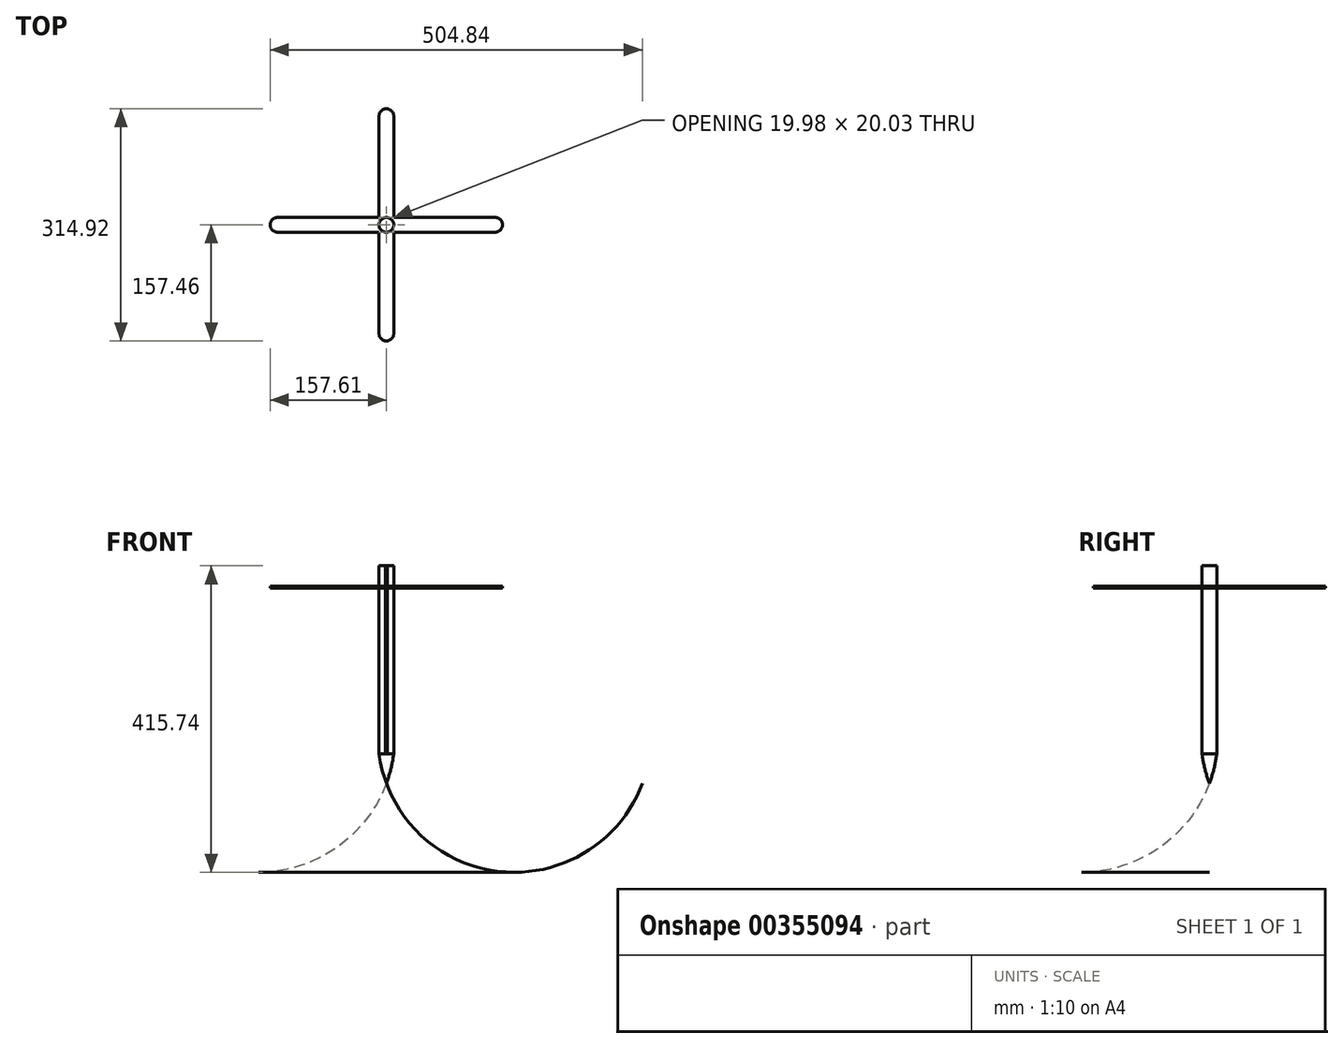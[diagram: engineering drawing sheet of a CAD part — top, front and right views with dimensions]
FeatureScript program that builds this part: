
annotation { "Feature Type Name" : "Feature", "Feature Type Description" : "" }
export const myFeature = defineFeature(function(context is Context, id is Id, definition is map)
    precondition{}
    {
        {
            var Q0;
            Q0=qCreatedBy(makeId("Top.planeOp"),FACE);
            var sketch = newSketch(context, id + "F0", { "sketchPlane" : qUnion([Q0])});
            skCircle(sketch, "E0", {"center": v(0, 0) * mm, "radius": 10.01 * mm});
            skLineSegment(sketch, "E1.bottom", {"start": v(0, 10.01) * mm, "end": v(147.64, 10.01) * mm});
            skLineSegment(sketch, "E1.top", {"start": v(0, -9.92) * mm, "end": v(147.64, -9.92) * mm});
            skLineSegment(sketch, "E1.left", {"start": v(0, 10.01) * mm, "end": v(0, -9.92) * mm});
            skLineSegment(sketch, "E1.right", {"start": v(147.64, 10.01) * mm, "end": v(147.64, -9.92) * mm});
            skLineSegment(sketch, "E2.MirrorCS", {"start": v(0, 10.01) * mm, "end": v(-147.64, 10.01) * mm});
            skLineSegment(sketch, "E3.MirrorCS", {"start": v(0, -9.92) * mm, "end": v(-147.64, -9.92) * mm});
            skLineSegment(sketch, "E4.MirrorCS", {"start": v(-147.64, 10.01) * mm, "end": v(-147.64, -9.92) * mm});
            skLineSegment(sketch, "E5", {"start": v(-10.01, 0) * mm, "end": v(-10.01, 147.44) * mm});
            skLineSegment(sketch, "E6", {"start": v(-10.01, 147.44) * mm, "end": v(10.01, 147.44) * mm});
            skLineSegment(sketch, "E7", {"start": v(10.01, 147.44) * mm, "end": v(10.01, 0) * mm});
            skLineSegment(sketch, "E8.MirrorCS", {"start": v(10.01, 147.44) * mm, "end": v(-10.01, 147.44) * mm});
            skLineSegment(sketch, "E9.MirrorCS", {"start": v(-10.01, -147.44) * mm, "end": v(10.01, -147.44) * mm});
            skLineSegment(sketch, "E10.MirrorCS", {"start": v(10.01, -147.44) * mm, "end": v(10.01, 0) * mm});
            skLineSegment(sketch, "E11.MirrorCS", {"start": v(-10.01, 0) * mm, "end": v(-10.01, -147.44) * mm});
            skArc(sketch, "E12", {"start": v(-147.64, 10.01) * mm, "mid": v(-157.61, 0.05) * mm, "end": v(-147.64, -9.92) * mm});
            skArc(sketch, "E13", {"start": v(-10.01, -147.44) * mm, "mid": v(0, -157.46) * mm, "end": v(10.01, -147.44) * mm});
            skArc(sketch, "E14.MirrorCS", {"start": v(147.64, 10.01) * mm, "mid": v(157.61, 0.05) * mm, "end": v(147.64, -9.92) * mm});
            skArc(sketch, "E15.MirrorCS", {"start": v(-10.01, 147.44) * mm, "mid": v(0, 157.46) * mm, "end": v(10.01, 147.44) * mm});
            skSolve(sketch);
        }
        {
            var Q0;
            {var subQ0=sQuery(id+"F0.wireOp",EDGE,"E1.left");Q0=makeQuery(id+"F0.imprint","IMPRINT",FACE,{"disambiguationData":[TD([[makeQuery(id+"F0.imprint","IMPRINT",EDGE,{"derivedFrom":subQ0}),-1.0]])]});}
            var Q1;
            {var subQ0=sQuery(id+"F0.wireOp",EDGE,"E1.left");Q1=makeQuery(id+"F0.imprint","IMPRINT",FACE,{"disambiguationData":[TD([[makeQuery(id+"F0.imprint","IMPRINT",EDGE,{"derivedFrom":subQ0}),1.0]])]});}
            extrude(context, id + "F1", {"entities" : qUnion([Q0, Q1]), "depth" : 30 * mm, "hasSecondDirection" : true, "secondDirectionOppositeDirection" : true, "secondDirectionDepth" : 225 * mm});
        }
        {
            var Q0;
            {var subQ5=sQuery(id+"F0.wireOp",EDGE,"E9.MirrorCS");Q0=makeQuery(id+"F0.imprint","IMPRINT",FACE,{"disambiguationData":[TD([[makeQuery(id+"F0.imprint","IMPRINT",EDGE,{"derivedFrom":subQ5}),1.0]])]});}
            var Q1;
            Q1=makeQuery(id+"F0.imprint","IMPRINT",FACE,{"disambiguationData":[TD([[makeQuery(id+"F0.imprint","IMPRINT",EDGE,{"derivedFrom":sQuery(id+"F0.wireOp",EDGE,"E9.MirrorCS")}),-1.0]])]});
            var Q2;
            Q2=makeQuery(id+"F0.imprint","IMPRINT",FACE,{"disambiguationData":[TD([[makeQuery(id+"F0.imprint","IMPRINT",EDGE,{"derivedFrom":sQuery(id+"F0.wireOp",EDGE,"E1.right")}),1.0]])]});
            var Q3;
            {var subQ1=sQuery(id+"F0.wireOp",EDGE,"E1.right");Q3=makeQuery(id+"F0.imprint","IMPRINT",FACE,{"disambiguationData":[TD([[makeQuery(id+"F0.imprint","IMPRINT",EDGE,{"derivedFrom":subQ1}),-1.0]])]});}
            var Q4;
            {var subQ0=sQuery(id+"F0.wireOp",EDGE,"E4.MirrorCS");Q4=makeQuery(id+"F0.imprint","IMPRINT",FACE,{"disambiguationData":[TD([[makeQuery(id+"F0.imprint","IMPRINT",EDGE,{"derivedFrom":subQ0}),1.0]])]});}
            var Q5;
            {var subQ1=sQuery(id+"F0.wireOp",EDGE,"E6");Q5=makeQuery(id+"F0.imprint","IMPRINT",FACE,{"disambiguationData":[TD([[makeQuery(id+"F0.imprint","IMPRINT",EDGE,{"derivedFrom":subQ1}),-1.0]])]});}
            var Q6;
            Q6=makeQuery(id+"F0.imprint","IMPRINT",FACE,{"disambiguationData":[TD([[makeQuery(id+"F0.imprint","IMPRINT",EDGE,{"derivedFrom":sQuery(id+"F0.wireOp",EDGE,"E6")}),1.0]])]});
            var Q7;
            Q7=makeQuery(id+"F0.imprint","IMPRINT",FACE,{"disambiguationData":[TD([[makeQuery(id+"F0.imprint","IMPRINT",EDGE,{"derivedFrom":sQuery(id+"F0.wireOp",EDGE,"E4.MirrorCS")}),-1.0]])]});
            var Q8;
            {var subQ0=sQuery(id+"F0.wireOp",EDGE,"E1.bottom");var subQ3=sQuery(id+"F0.wireOp",EDGE,"E7");var subQ5=makeQuery(id+"F0.imprint","INTERSECT",VERTEX,{"derivedFrom":[subQ0,subQ3]});Q8=makeQuery(id+"F0.imprint","IMPRINT",FACE,{"disambiguationData":[TD([[makeQuery(id+"F0.imprint","IMPRINT",EDGE,{"disambiguationData":[TD([[subQ5,-1.0]])],"derivedFrom":subQ3}),-1.0]])]});}
            var Q9;
            {var subQ0=sQuery(id+"F0.wireOp",EDGE,"E2.MirrorCS");var subQ3=sQuery(id+"F0.wireOp",EDGE,"E5");var subQ5=makeQuery(id+"F0.imprint","INTERSECT",VERTEX,{"derivedFrom":[subQ0,subQ3]});Q9=makeQuery(id+"F0.imprint","IMPRINT",FACE,{"disambiguationData":[TD([[makeQuery(id+"F0.imprint","IMPRINT",EDGE,{"disambiguationData":[TD([[subQ5,1.0]])],"derivedFrom":subQ3}),-1.0]])]});}
            var Q10;
            {var subQ0=sQuery(id+"F0.wireOp",EDGE,"E11.MirrorCS");var subQ3=sQuery(id+"F0.wireOp",EDGE,"E3.MirrorCS");var subQ5=makeQuery(id+"F0.imprint","INTERSECT",VERTEX,{"derivedFrom":[subQ3,subQ0]});Q10=makeQuery(id+"F0.imprint","IMPRINT",FACE,{"disambiguationData":[TD([[makeQuery(id+"F0.imprint","IMPRINT",EDGE,{"disambiguationData":[TD([[subQ5,1.0]])],"derivedFrom":subQ3}),-1.0]])]});}
            var Q11;
            {var subQ0=sQuery(id+"F0.wireOp",EDGE,"E10.MirrorCS");var subQ3=sQuery(id+"F0.wireOp",EDGE,"E1.top");var subQ5=makeQuery(id+"F0.imprint","INTERSECT",VERTEX,{"derivedFrom":[subQ3,subQ0]});Q11=makeQuery(id+"F0.imprint","IMPRINT",FACE,{"disambiguationData":[TD([[makeQuery(id+"F0.imprint","IMPRINT",EDGE,{"disambiguationData":[TD([[subQ5,1.0]])],"derivedFrom":subQ3}),1.0]])]});}
            extrude(context, id + "F2", {"entities" : qUnion([Q0, Q1, Q2, Q3, Q4, Q5, Q6, Q7, Q8, Q9, Q10, Q11]), "operationType" : NewBodyOperationType.ADD, "depth" : 2 * mm});
        }
        {
            var Q0;
            Q0=qCreatedBy(makeId("Front.planeOp"),FACE);
            var sketch = newSketch(context, id + "F3", { "sketchPlane" : qUnion([Q0])});
            skLineSegment(sketch, "E16", {"start": v(0, -224.96) * mm, "end": v(0, -265.1) * mm});
            skLineSegment(sketch, "E17", {"start": v(0, -265.1) * mm, "end": v(-10, -225) * mm});
            skLineSegment(sketch, "E18", {"start": v(-10, -225) * mm, "end": v(0, -224.96) * mm});
            skArc(sketch, "E19", {"start": v(-10, -225) * mm, "mid": v(-6.13, -245.33) * mm, "end": v(0, -265.1) * mm});
            skSolve(sketch);
        }
        {
            var Q0;
            Q0=makeQuery(id+"F3.imprint","IMPRINT",FACE,{"disambiguationData":[TD([[makeQuery(id+"F3.imprint","IMPRINT",EDGE,{"derivedFrom":sQuery(id+"F3.wireOp",EDGE,"E16")}),-1.0]])]});
            var Q1;
            Q1=makeQuery(id+"F3.imprint","IMPRINT",FACE,{"disambiguationData":[TD([[makeQuery(id+"F3.imprint","IMPRINT",EDGE,{"derivedFrom":sQuery(id+"F3.wireOp",EDGE,"E17")}),1.0]])]});
            var Q2;
            Q2=sQuery(id+"F3.wireOp",EDGE,"E16");
            revolve(context, id + "F4", {"operationType" : NewBodyOperationType.ADD, "entities" : qUnion([Q0, Q1]), "axis" : qUnion([Q2]), "revolveType" : RevolveType.FULL});
        }
    });
